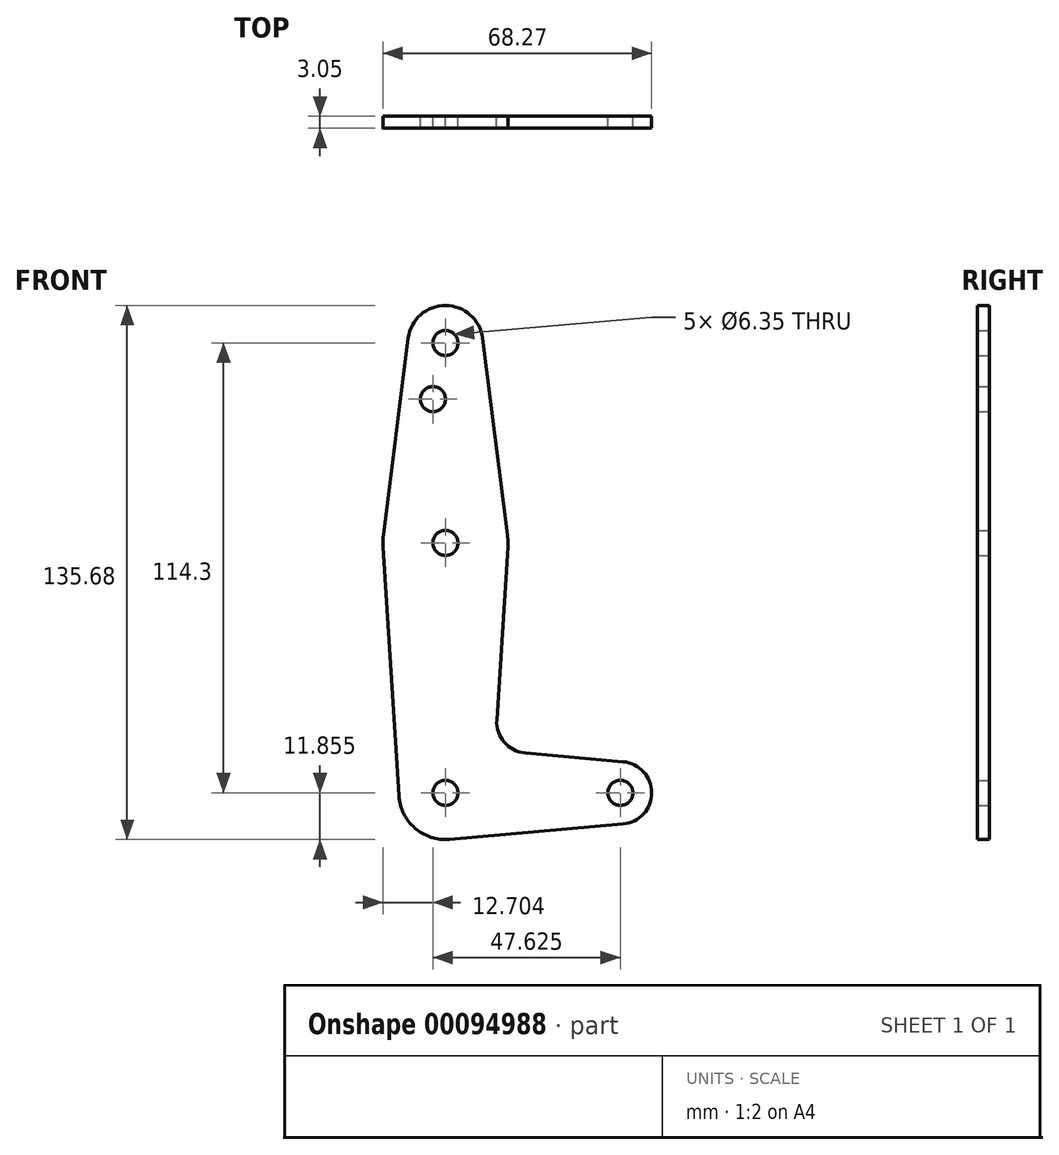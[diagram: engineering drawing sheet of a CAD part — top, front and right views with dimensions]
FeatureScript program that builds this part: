
annotation { "Feature Type Name" : "Feature", "Feature Type Description" : "" }
export const myFeature = defineFeature(function(context is Context, id is Id, definition is map)
    precondition{}
    {
        {
            var Q0;
            Q0=qCreatedBy(makeId("Front.planeOp"),FACE);
            var sketch = newSketch(context, id + "F0", { "sketchPlane" : qUnion([Q0])});
            skLineSegment(sketch, "E0", {"start": v(-15.75, 98.74) * mm, "end": v(-15.75, -15.56) * mm, "construction": true});
            skLineSegment(sketch, "E1", {"start": v(-15.75, -15.56) * mm, "end": v(28.7, -15.56) * mm, "construction": true});
            skCircle(sketch, "E2", {"center": v(-15.75, 98.74) * mm, "radius": 9.53 * mm});
            skCircle(sketch, "E3", {"center": v(-15.75, 47.94) * mm, "radius": 15.88 * mm});
            skCircle(sketch, "E4", {"center": v(-15.75, -15.56) * mm, "radius": 11.85 * mm});
            skCircle(sketch, "E5", {"center": v(28.7, -15.56) * mm, "radius": 7.94 * mm});
            skLineSegment(sketch, "E6", {"start": v(-25.2, 99.94) * mm, "end": v(-31.5, 49.93) * mm});
            skLineSegment(sketch, "E7", {"start": v(-6.3, 99.94) * mm, "end": v(0, 49.93) * mm});
            skLineSegment(sketch, "E8", {"start": v(-3.92, -16.3) * mm, "end": v(-3.87, -15.56) * mm});
            skLineSegment(sketch, "E9", {"start": v(-31.6, 46.94) * mm, "end": v(-27.58, -16.3) * mm});
            skLineSegment(sketch, "E10", {"start": v(29.4, -7.65) * mm, "end": v(4.54, -5.45) * mm});
            skLineSegment(sketch, "E11", {"start": v(-14.7, -27.36) * mm, "end": v(29.4, -23.46) * mm});
            skCircle(sketch, "E12", {"center": v(-15.75, 98.74) * mm, "radius": 3.18 * mm});
            skCircle(sketch, "E13", {"center": v(-15.75, 47.94) * mm, "radius": 3.18 * mm});
            skCircle(sketch, "E14", {"center": v(-15.75, -15.56) * mm, "radius": 3.18 * mm});
            skCircle(sketch, "E15", {"center": v(28.7, -15.56) * mm, "radius": 3.18 * mm});
            skCircle(sketch, "E16", {"center": v(-18.93, 84.47) * mm, "radius": 3.18 * mm});
            skLineSegment(sketch, "E17.trimOffspring", {"start": v(-2.7, 2.97) * mm, "end": v(0.1, 46.94) * mm});
            skPoint(sketch, "E18.visualSharp", {"position": v(-3.19, -4.77) * mm});
            skArc(sketch, "E18.filletArc", {"start": v(-2.7, 2.97) * mm, "mid": v(-0.8, -2.71) * mm, "end": v(4.54, -5.45) * mm});
            skSolve(sketch);
        }
        {
            var Q0;
            Q0=makeQuery(id+"F0.imprint","IMPRINT",FACE,{"disambiguationData":[TD([[makeQuery(id+"F0.imprint","IMPRINT",EDGE,{"derivedFrom":sQuery(id+"F0.wireOp",EDGE,"E13")}),-1.0]])]});
            var Q1;
            {var subQ1=sQuery(id+"F0.wireOp",EDGE,"E6");Q1=makeQuery(id+"F0.imprint","IMPRINT",FACE,{"disambiguationData":[TD([[makeQuery(id+"F0.imprint","IMPRINT",EDGE,{"derivedFrom":subQ1}),1.0]])]});}
            var Q2;
            Q2=makeQuery(id+"F0.imprint","IMPRINT",FACE,{"disambiguationData":[TD([[makeQuery(id+"F0.imprint","IMPRINT",EDGE,{"derivedFrom":sQuery(id+"F0.wireOp",EDGE,"E12")}),-1.0]])]});
            var Q3;
            Q3=makeQuery(id+"F0.imprint","IMPRINT",FACE,{"disambiguationData":[TD([[makeQuery(id+"F0.imprint","IMPRINT",EDGE,{"derivedFrom":sQuery(id+"F0.wireOp",EDGE,"E14")}),-1.0]])]});
            var Q4;
            {var subQ5=sQuery(id+"F0.wireOp",EDGE,"E9");Q4=makeQuery(id+"F0.imprint","IMPRINT",FACE,{"disambiguationData":[TD([[makeQuery(id+"F0.imprint","IMPRINT",EDGE,{"derivedFrom":subQ5}),1.0]])]});}
            var Q5;
            Q5=makeQuery(id+"F0.imprint","IMPRINT",FACE,{"disambiguationData":[TD([[makeQuery(id+"F0.imprint","IMPRINT",EDGE,{"derivedFrom":sQuery(id+"F0.wireOp",EDGE,"E15")}),-1.0]])]});
            extrude(context, id + "F1", {"entities" : qUnion([Q0, Q1, Q2, Q3, Q4, Q5]), "depth" : 3.05 * mm});
        }
    });
